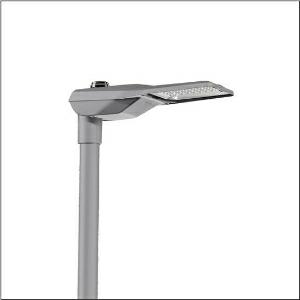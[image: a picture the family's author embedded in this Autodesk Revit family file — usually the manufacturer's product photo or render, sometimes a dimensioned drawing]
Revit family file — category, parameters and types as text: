
# Revit family: streetlight_sl_21_mini___st0_5a_5xe6b37n08jb_3e92
name_source: partatom
category: Lighting Fixtures
units: mm (PartAtom-declared; Revit-internal decimal feet)

## family parameters
Cut with Voids When Loaded = No
Host = Face
Light Source = No
Part Type = Normal
Room Calculation Point = No
Round Connector Dimension = Use Diameter
Shared = No

## types (1)
- --- (1 x LED, 12830 lm, 87.3 W, 3000K)
    Apparent Load = 87 VA
    CIE Flux Codes = 43 76 97 100 100
    Color Rendering = 70
    Color Temperature = 3000K
    Default Elevation = 1800 mm
    Description = Streetlight SL 21 mini, mast luminaire, primary light control with lens, of PMMA, primary optical cover: cover, of toughened safety glass, transparent, light distribution: ST0.5a, light emission: direct distribution, primary light characteristic: asymmetric, installation type: side-entry, LED, 3G 2.5mm², High Power LED, rated luminous flux: 12.830lm, luminous efficacy: 147lm/W, light colour: 730, colour temperature: 3000K, control gear: NEMA (7pin), control: overheat protection, pre-setting: linear dimming characteristic, constant luminous flux control, time-dependent luminous flux control, flexible luminous flux parameterisation, mains connection: 230..240V, AC, 50/60Hz, connection cable pre-assembled, cable length: 10,5m, wiring characteristics: H05VV-F, start of lifetime: 87W, end of service life: 90W, reduction: 40W, luminaire housing, of diecast aluminium (EN AC-44300), powder-coated, SITECO metallic grey (DB 702S), corrosivity category C5 high according to DIN EN ISO 12944, multi-level sealing system, sealing non-destructively replaceable, inclination adjustable: 0°, 5°, 10°, 15°, length: 628mm, width: 235mm, height: 110mm, spigot size: 42mm (side-entry), mounting height: 4..8m, protection rating (complete): IP66, insulation class (complete): insulation class I (protective earthing), certification: CE, ENEC, ENEC+, VDE, impact resistance: IK10, permissible operating ambient temperature for outdoor applications: -40..+50°C, standard-compliant lighting for roads and squares, packaging unit: 1 piece

Light Distribution: ST0.5a
    Height = 110 mm
    Lamp = 1 x LED
    Lamp Light Flux = 12830 lm
    Lamp Power = 87.3 W
    Lamp count = 1
    Length = 625 mm
    Luminous efficacy = 147 lm/W
    Manufacturer = Siteco
    ModVariant = No
    Model = 5XE6B37N08JB
    Number of Poles = 1
    OnlyDefault = Yes
    Power Factor = 1
    Product Name = Streetlight SL 21 mini | ST0.5a
    Product group = mast luminaire | pylon top
    ProductGroupID = 6100
    Protection Class = Protection class I
    Protection Degree = IP 66
    RLX_Detail_Level = 1
    RLX_Emergency_Light_Flux = 0 lm
    RLX_Emergency_Type = 0
    RLX_Emergency_Type_DB = No
    RlxData = <blob elided: 37265 chars, md5=6283533a>
    Socket = socket
    Standby Power = 0 W
    System Light Flux = 12830 lm
    System Power = 87 W
    Type Comments = factory setting: luminous flux: 100 % | dim-lin: 254 | 915 mA
    Type Image = l_1294379.jpg
    URL = http://relux.com
    VarID = @adj_136265
    Voltage = 0 V
    Weight = 0.00 kg
    Width = 234 mm

## geometry (parser evidence)
native form markers: Blend x4, Sweep x12
no freeform markers — native parametric forms only
